# Revit family: Valve-Wall_Mount-KALLISTA-Italy-P32716_1
name_source: partatom
category: Plumbing Fixtures
units: mm (PartAtom-declared; Revit-internal decimal feet)

## family parameters
Cut with Voids When Loaded = No
Host = Face
OmniClass Number = 23.27.31.00
Part Type = Normal
Room Calculation Point = No
Round Connector Dimension = Use Diameter
Shared = No

## types (1)
- NA-Brass
    ADA Compliant = No
    Assembly Code = D2020
    CW Connection = Yes
    Cold Water Inlet = Cold Water Inlet
    Date Modified = 10/26/2024
    Default Elevation = 36"
    Description = Single Control Wall Mount Rough In Valve
    Finish = Kohler-Metal-Brass
    Flow Rate = 0 GPM
    HW Connection = Yes
    Height = 2 11/16"
    Hot Water Inlet = Hot Water Inlet
    Length = 2 3/16"
    Manufacturer = Kallista Co.
    Master Format 2014 = 23 09 13.33
    Master Format 2014 Name = Control Valves
    Material = Premium Metal Construction
    Model = P32716-00-NA
    Pressure = 0.00 psi
    Product Name = Italy
    Tempered Water Outlet = Tempered Water Outlet
    Type = 1
    URL = https://www.kallista.com
    Vent Connection = No
    Waste Connection = No
    Waste Water Outlet = Waste Water Outlet
    WaterSense Certified = No
    Width = 7 15/16"

## geometry (parser evidence)
native form markers: Sweep x4
no freeform markers — native parametric forms only
